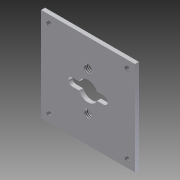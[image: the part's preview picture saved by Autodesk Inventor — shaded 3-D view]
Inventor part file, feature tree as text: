
AUTODESK INVENTOR PART (.ipt)
format: ipt  version: 2012 (Build 160160000, 160)  size: 115,200 bytes
history: native  units: in
note: dims shown in document units (in); Inventor stores cm internally (conversion verified against a paired STEP export)
features: extrude x2, thread x2, sketch x1, hole x1
ambient origin geometry x8: Origin, YZ Plane, XZ Plane, XY Plane, X Axis, Y Axis, Z Axis, Center Point
bodies: Solid1 (feature_tree)
feature tree (6):
  sketch  "Sketch1"  dims[d0=3.0in d1=3.0in d2=1.5in d3=1.5in d4=0.625in d5=0.25in d6=0.25in d7=0.25in d8=0.25in d10=0.125in d11=0.0in d12=0.156in d13=0.75in d14=0.375in d15=0.25in d16=0.5635in d17=1.0in d18=0.8108in d36=0.5in d37=0.5in d42=0.25in d43=1.1in d44=0.125in d45=0.55in d46=0.25in d47=0.25in d48=0.625in d49=1.25in d50=1.0in d51=0.0in d52=1.0in d53=0.0in d54=1.0in d55=0.0in]
  extrude  "Extrusion1"  Depth=3.0in
  hole  "Hole1"  [1 undecoded]
  extrude  "Extrusion3"  Depth=1.5in
  thread  "Thread1"  [1 undecoded]
  thread  "Thread2"  [1 undecoded]
note: 3 required parameter values undecoded (feature->parameter linkage not recoverable at this tier; creation-order binding heuristic only, values carry confidence <= 0.55)
